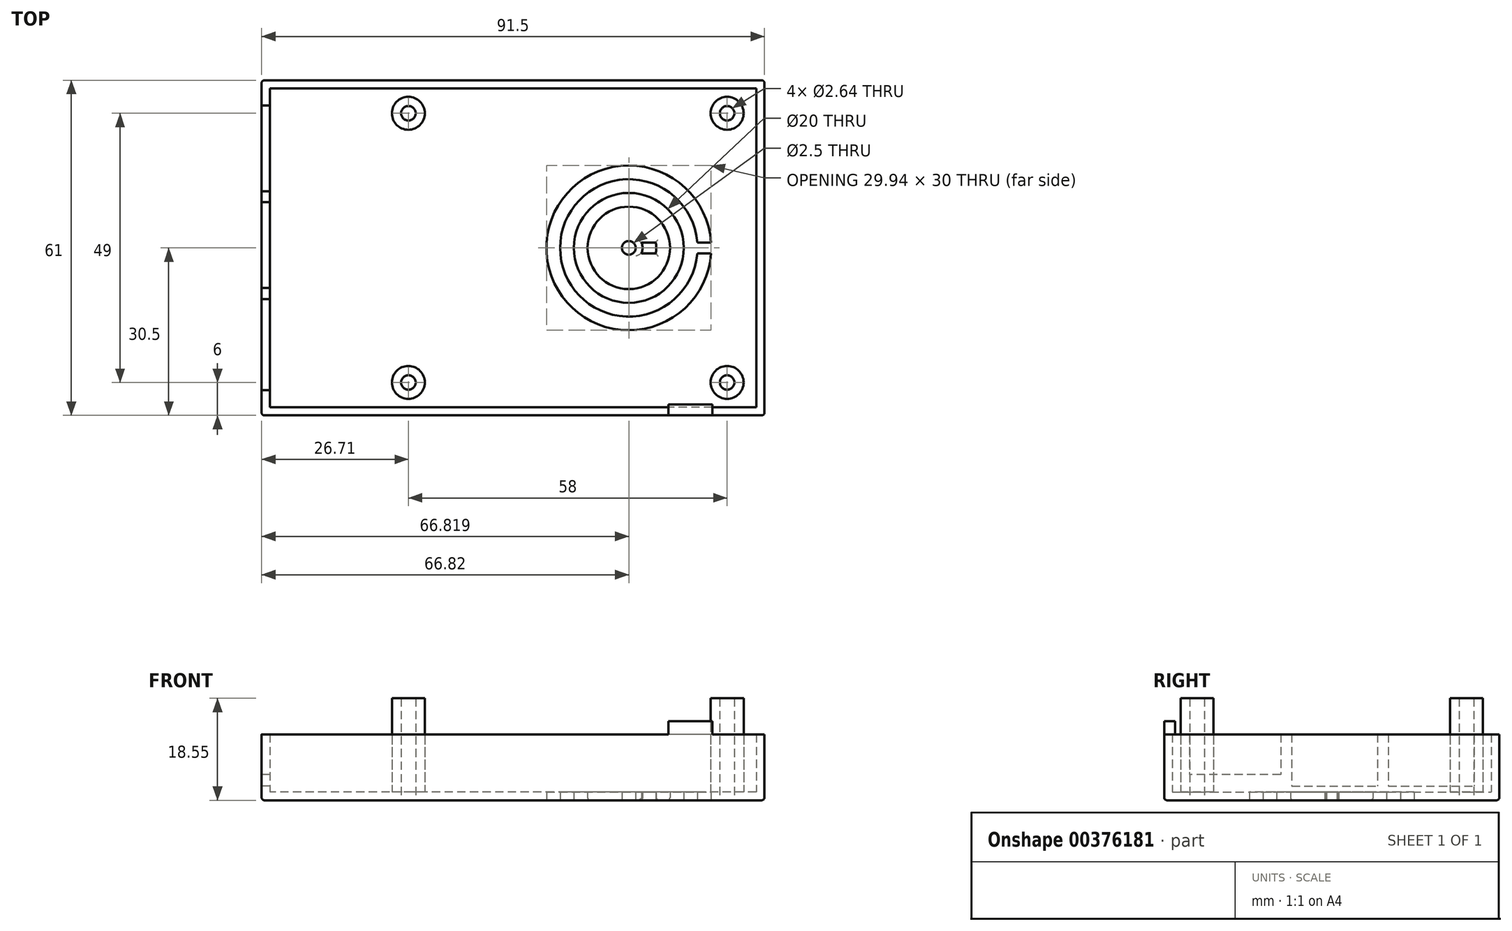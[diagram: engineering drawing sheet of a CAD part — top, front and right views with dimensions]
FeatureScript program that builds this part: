
annotation { "Feature Type Name" : "Feature", "Feature Type Description" : "" }
export const myFeature = defineFeature(function(context is Context, id is Id, definition is map)
    precondition{}
    {
        {
            var Q0;
            Q0=qCreatedBy(makeId("Top.planeOp"),FACE);
            var sketch = newSketch(context, id + "F0", { "sketchPlane" : qUnion([Q0])});
            skLineSegment(sketch, "E0.bottom", {"start": v(45.75, -30.5) * mm, "end": v(-45.75, -30.5) * mm});
            skLineSegment(sketch, "E0.top", {"start": v(45.75, 30.5) * mm, "end": v(-45.75, 30.5) * mm});
            skLineSegment(sketch, "E0.left", {"start": v(45.75, -30.5) * mm, "end": v(45.75, 30.5) * mm});
            skLineSegment(sketch, "E0.right", {"start": v(-45.75, -30.5) * mm, "end": v(-45.75, 30.5) * mm});
            skPoint(sketch, "E0.middle", {"position": v(0, 0) * mm});
            skSolve(sketch);
        }
        {
            var Q0;
            Q0 = qSketchRegion(id + "F0", true);
            extrude(context, id + "F1", {"entities" : qUnion([Q0]), "depth" : 12 * mm});
        }
        {
            var Q0;
            Q0=makeQuery(id+"F1.opExtrude","CAP_FACE",FACE,{"disambiguationData":[OSD([sQuery(id+"F0.wireOp",EDGE,"E0.bottom"),sQuery(id+"F0.wireOp",EDGE,"E0.top"),sQuery(id+"F0.wireOp",EDGE,"E0.left"),sQuery(id+"F0.wireOp",EDGE,"E0.right")])],"isStart":false});
            shell(context, id + "F2", {"entities" : qUnion([Q0]), "thickness" : 1.5 * mm});
        }
        {
            var Q0;
            Q0=makeQuery(id+"F1.opExtrude","SWEPT_FACE",FACE,{"disambiguationData":[OSD([sQuery(id+"F0.wireOp",EDGE,"E0.bottom")])]});
            var sketch = newSketch(context, id + "F3", { "sketchPlane" : qUnion([Q0])});
            skLineSegment(sketch, "E1.bottom", {"start": v(36.25, 12) * mm, "end": v(28.25, 12) * mm});
            skLineSegment(sketch, "E1.top", {"start": v(36.25, 14.4) * mm, "end": v(28.25, 14.4) * mm});
            skLineSegment(sketch, "E1.left", {"start": v(36.25, 12) * mm, "end": v(36.25, 14.4) * mm});
            skLineSegment(sketch, "E1.right", {"start": v(28.25, 12) * mm, "end": v(28.25, 14.4) * mm});
            skSolve(sketch);
        }
        {
            var Q0;
            Q0 = qSketchRegion(id + "F3", true);
            extrude(context, id + "F4", {"entities" : qUnion([Q0]), "operationType" : NewBodyOperationType.ADD, "oppositeDirection" : true, "depth" : 2 * mm});
        }
        {
            var Q0;
            Q0=makeQuery(id+"F1.opExtrude","SWEPT_FACE",FACE,{"disambiguationData":[OSD([sQuery(id+"F0.wireOp",EDGE,"E0.right")])]});
            var sketch = newSketch(context, id + "F5", { "sketchPlane" : qUnion([Q0])});
            skLineSegment(sketch, "E2.bottom", {"start": v(9.3, 12) * mm, "end": v(25.9, 12) * mm});
            skLineSegment(sketch, "E2.top", {"start": v(9.3, 4.7) * mm, "end": v(25.9, 4.7) * mm});
            skLineSegment(sketch, "E2.left", {"start": v(9.3, 12) * mm, "end": v(9.3, 4.7) * mm});
            skLineSegment(sketch, "E2.right", {"start": v(25.9, 12) * mm, "end": v(25.9, 4.7) * mm});
            skLineSegment(sketch, "E3.bottom", {"start": v(7.3, 12) * mm, "end": v(-8.3, 12) * mm});
            skLineSegment(sketch, "E3.top", {"start": v(7.3, 2.6) * mm, "end": v(-8.3, 2.6) * mm});
            skLineSegment(sketch, "E3.left", {"start": v(7.3, 12) * mm, "end": v(7.3, 2.6) * mm});
            skLineSegment(sketch, "E3.right", {"start": v(-8.3, 12) * mm, "end": v(-8.3, 2.6) * mm});
            skLineSegment(sketch, "E4.bottom", {"start": v(-10.3, 12) * mm, "end": v(-25.9, 12) * mm});
            skLineSegment(sketch, "E4.top", {"start": v(-10.3, 2.6) * mm, "end": v(-25.9, 2.6) * mm});
            skLineSegment(sketch, "E4.left", {"start": v(-10.3, 12) * mm, "end": v(-10.3, 2.6) * mm});
            skLineSegment(sketch, "E4.right", {"start": v(-25.9, 12) * mm, "end": v(-25.9, 2.6) * mm});
            skSolve(sketch);
        }
        {
            var Q0;
            Q0 = qSketchRegion(id + "F5", true);
            extrude(context, id + "F6", {"entities" : qUnion([Q0]), "operationType" : NewBodyOperationType.REMOVE, "oppositeDirection" : true, "depth" : 2.1 * mm});
        }
        {
            var Q0;
            Q0=makeQuery(id+"F1.opExtrude","CAP_FACE",FACE,{"disambiguationData":[OSD([sQuery(id+"F0.wireOp",EDGE,"E0.bottom"),sQuery(id+"F0.wireOp",EDGE,"E0.top"),sQuery(id+"F0.wireOp",EDGE,"E0.left"),sQuery(id+"F0.wireOp",EDGE,"E0.right")])],"isStart":true});
            var sketch = newSketch(context, id + "F7", { "sketchPlane" : qUnion([Q0])});
            skCircle(sketch, "E5", {"center": v(21.07, 0) * mm, "radius": 2.5 * mm});
            skCircle(sketch, "E6", {"center": v(21.07, 0) * mm, "radius": 5 * mm});
            skCircle(sketch, "E7", {"center": v(21.07, 0) * mm, "radius": 7.5 * mm});
            skCircle(sketch, "E8", {"center": v(21.07, 0) * mm, "radius": 10 * mm});
            skCircle(sketch, "E9", {"center": v(21.07, 0) * mm, "radius": 12.5 * mm});
            skCircle(sketch, "E10", {"center": v(21.07, 0) * mm, "radius": 15 * mm});
            skLineSegment(sketch, "E11.bottom", {"start": v(36.04, 0.99) * mm, "end": v(33.53, 0.99) * mm});
            skLineSegment(sketch, "E11.top", {"start": v(36.04, -0.99) * mm, "end": v(33.53, -0.99) * mm});
            skLineSegment(sketch, "E11.left", {"start": v(36.04, 0.99) * mm, "end": v(36.04, -0.99) * mm});
            skLineSegment(sketch, "E11.right", {"start": v(6.1, 0.99) * mm, "end": v(6.1, -0.99) * mm});
            skLineSegment(sketch, "E12.trimOffspring", {"start": v(8.6, 0.99) * mm, "end": v(6.1, 0.99) * mm});
            skLineSegment(sketch, "E13.trimOffspring", {"start": v(8.6, -0.99) * mm, "end": v(6.1, -0.99) * mm});
            skLineSegment(sketch, "E14.trimOffspring", {"start": v(31.02, 0.99) * mm, "end": v(11.12, 0.99) * mm});
            skLineSegment(sketch, "E15.trimOffspring", {"start": v(31.02, -0.99) * mm, "end": v(11.12, -0.99) * mm});
            skSolve(sketch);
        }
        {
            var Q0;
            {var subQ0=sQuery(id+"F7.wireOp",EDGE,"E11.bottom");Q0=makeQuery(id+"F7.imprint","IMPRINT",FACE,{"disambiguationData":[TD([[makeQuery(id+"F7.imprint","IMPRINT",EDGE,{"derivedFrom":subQ0}),-1.0]])]});}
            var Q1;
            {var subQ0=sQuery(id+"F7.wireOp",EDGE,"E11.top");Q1=makeQuery(id+"F7.imprint","IMPRINT",FACE,{"disambiguationData":[TD([[makeQuery(id+"F7.imprint","IMPRINT",EDGE,{"derivedFrom":subQ0}),1.0]])]});}
            var Q2;
            {var subQ0=sQuery(id+"F7.wireOp",EDGE,"E14.trimOffspring");var subQ1=sQuery(id+"F7.wireOp",EDGE,"E7");var subQ2=makeQuery(id+"F7.imprint","INTERSECT",VERTEX,{"disambiguationData":[OD(0.0)],"derivedFrom":[subQ1,subQ0]});Q2=makeQuery(id+"F7.imprint","IMPRINT",FACE,{"disambiguationData":[TD([[makeQuery(id+"F7.imprint","IMPRINT",EDGE,{"disambiguationData":[TD([[subQ2,1.0]])],"derivedFrom":subQ1}),-1.0]])]});}
            var Q3;
            {var subQ0=sQuery(id+"F7.wireOp",EDGE,"E15.trimOffspring");var subQ1=sQuery(id+"F7.wireOp",EDGE,"E7");var subQ2=makeQuery(id+"F7.imprint","INTERSECT",VERTEX,{"disambiguationData":[OD(0.0)],"derivedFrom":[subQ1,subQ0]});Q3=makeQuery(id+"F7.imprint","IMPRINT",FACE,{"disambiguationData":[TD([[makeQuery(id+"F7.imprint","IMPRINT",EDGE,{"disambiguationData":[TD([[subQ2,-1.0]])],"derivedFrom":subQ1}),-1.0]])]});}
            var Q4;
            {var subQ0=sQuery(id+"F7.wireOp",EDGE,"E14.trimOffspring");var subQ1=sQuery(id+"F7.wireOp",EDGE,"E5");var subQ2=makeQuery(id+"F7.imprint","INTERSECT",VERTEX,{"disambiguationData":[OD(0.0)],"derivedFrom":[subQ1,subQ0]});Q4=makeQuery(id+"F7.imprint","IMPRINT",FACE,{"disambiguationData":[TD([[makeQuery(id+"F7.imprint","IMPRINT",EDGE,{"disambiguationData":[TD([[subQ2,1.0]])],"derivedFrom":subQ1}),-1.0]])]});}
            var Q5;
            {var subQ0=sQuery(id+"F7.wireOp",EDGE,"E15.trimOffspring");var subQ1=sQuery(id+"F7.wireOp",EDGE,"E5");var subQ2=makeQuery(id+"F7.imprint","INTERSECT",VERTEX,{"disambiguationData":[OD(0.0)],"derivedFrom":[subQ1,subQ0]});Q5=makeQuery(id+"F7.imprint","IMPRINT",FACE,{"disambiguationData":[TD([[makeQuery(id+"F7.imprint","IMPRINT",EDGE,{"disambiguationData":[TD([[subQ2,-1.0]])],"derivedFrom":subQ1}),-1.0]])]});}
            extrude(context, id + "F8", {"entities" : qUnion([Q0, Q1, Q2, Q3, Q4, Q5]), "operationType" : NewBodyOperationType.REMOVE, "oppositeDirection" : true, "depth" : 3 * mm});
        }
        {
            var Q0;
            Q0=makeQuery(id+"F1.opExtrude","CAP_FACE",FACE,{"disambiguationData":[OSD([sQuery(id+"F0.wireOp",EDGE,"E0.bottom"),sQuery(id+"F0.wireOp",EDGE,"E0.top"),sQuery(id+"F0.wireOp",EDGE,"E0.left"),sQuery(id+"F0.wireOp",EDGE,"E0.right")])],"isStart":true});
            var sketch = newSketch(context, id + "F9", { "sketchPlane" : qUnion([Q0])});
            skCircle(sketch, "E16", {"center": v(21.07, 0) * mm, "radius": 1.25 * mm});
            skSolve(sketch);
        }
        {
            var Q0;
            Q0 = qSketchRegion(id + "F9", true);
            extrude(context, id + "F10", {"entities" : qUnion([Q0]), "operationType" : NewBodyOperationType.REMOVE, "oppositeDirection" : true, "depth" : 3 * mm});
        }
        {
            var Q0;
            Q0=makeQuery(id+"F2.opShell","OFFSET_FACE",FACE,{"disambiguationData":[OSD([sQuery(id+"F0.wireOp",EDGE,"E0.bottom"),sQuery(id+"F0.wireOp",EDGE,"E0.top"),sQuery(id+"F0.wireOp",EDGE,"E0.left"),sQuery(id+"F0.wireOp",EDGE,"E0.right")])]});
            var sketch = newSketch(context, id + "F11", { "sketchPlane" : qUnion([Q0])});
            skCircle(sketch, "E17", {"center": v(38.96, 24.5) * mm, "radius": 3 * mm});
            skCircle(sketch, "E18", {"center": v(38.96, 24.5) * mm, "radius": 1.32 * mm});
            skCircle(sketch, "E19", {"center": v(38.96, -24.5) * mm, "radius": 3 * mm});
            skCircle(sketch, "E20", {"center": v(38.96, -24.5) * mm, "radius": 1.32 * mm});
            skCircle(sketch, "E21", {"center": v(-19.04, 24.5) * mm, "radius": 3 * mm});
            skCircle(sketch, "E22", {"center": v(-19.04, 24.5) * mm, "radius": 1.32 * mm});
            skCircle(sketch, "E23", {"center": v(-19.04, -24.5) * mm, "radius": 3 * mm});
            skCircle(sketch, "E24", {"center": v(-19.04, -24.5) * mm, "radius": 1.32 * mm});
            skSolve(sketch);
        }
        {
            var Q0;
            Q0 = qSketchRegion(id + "F11", true);
            extrude(context, id + "F12", {"entities" : qUnion([Q0]), "operationType" : NewBodyOperationType.ADD, "depth" : 17.05 * mm});
        }
        {
            var Q0;
            Q0=makeQuery(id+"F12.boolean.opBoolean","SPLIT",FACE,{"disambiguationData":[TD([makeQuery(id+"F12.opExtrude","SWEPT_FACE",FACE,{"disambiguationData":[OSD([sQuery(id+"F11.wireOp",EDGE,"E18")])]})])],"derivedFrom":makeQuery(id+"F2.opShell","OFFSET_FACE",FACE,{"disambiguationData":[OSD([sQuery(id+"F0.wireOp",EDGE,"E0.bottom"),sQuery(id+"F0.wireOp",EDGE,"E0.top"),sQuery(id+"F0.wireOp",EDGE,"E0.left"),sQuery(id+"F0.wireOp",EDGE,"E0.right")])]})});
            var Q1;
            Q1=makeQuery(id+"F12.boolean.opBoolean","SPLIT",FACE,{"disambiguationData":[TD([makeQuery(id+"F12.opExtrude","SWEPT_FACE",FACE,{"disambiguationData":[OSD([sQuery(id+"F11.wireOp",EDGE,"E20")])]})])],"derivedFrom":makeQuery(id+"F2.opShell","OFFSET_FACE",FACE,{"disambiguationData":[OSD([sQuery(id+"F0.wireOp",EDGE,"E0.bottom"),sQuery(id+"F0.wireOp",EDGE,"E0.top"),sQuery(id+"F0.wireOp",EDGE,"E0.left"),sQuery(id+"F0.wireOp",EDGE,"E0.right")])]})});
            var Q2;
            Q2=makeQuery(id+"F12.boolean.opBoolean","SPLIT",FACE,{"disambiguationData":[TD([makeQuery(id+"F12.opExtrude","SWEPT_FACE",FACE,{"disambiguationData":[OSD([sQuery(id+"F11.wireOp",EDGE,"E24")])]})])],"derivedFrom":makeQuery(id+"F2.opShell","OFFSET_FACE",FACE,{"disambiguationData":[OSD([sQuery(id+"F0.wireOp",EDGE,"E0.bottom"),sQuery(id+"F0.wireOp",EDGE,"E0.top"),sQuery(id+"F0.wireOp",EDGE,"E0.left"),sQuery(id+"F0.wireOp",EDGE,"E0.right")])]})});
            var Q3;
            Q3=makeQuery(id+"F12.boolean.opBoolean","SPLIT",FACE,{"disambiguationData":[TD([makeQuery(id+"F12.opExtrude","SWEPT_FACE",FACE,{"disambiguationData":[OSD([sQuery(id+"F11.wireOp",EDGE,"E22")])]})])],"derivedFrom":makeQuery(id+"F2.opShell","OFFSET_FACE",FACE,{"disambiguationData":[OSD([sQuery(id+"F0.wireOp",EDGE,"E0.bottom"),sQuery(id+"F0.wireOp",EDGE,"E0.top"),sQuery(id+"F0.wireOp",EDGE,"E0.left"),sQuery(id+"F0.wireOp",EDGE,"E0.right")])]})});
            extrude(context, id + "F13", {"entities" : qUnion([Q0, Q1, Q2, Q3]), "operationType" : NewBodyOperationType.REMOVE, "oppositeDirection" : true, "depth" : 25 * mm});
        }
        {
            var Q0;
            Q0=makeQuery(id+"F1.opExtrude","CAP_EDGE",EDGE,{"disambiguationData":[OSD([sQuery(id+"F0.wireOp",EDGE,"E0.top")])],"isStart":true});
            var Q1;
            Q1=makeQuery(id+"F1.opExtrude","CAP_EDGE",EDGE,{"disambiguationData":[OSD([sQuery(id+"F0.wireOp",EDGE,"E0.left")])],"isStart":true});
            var Q2;
            Q2=makeQuery(id+"F1.opExtrude","CAP_EDGE",EDGE,{"disambiguationData":[OSD([sQuery(id+"F0.wireOp",EDGE,"E0.bottom")])],"isStart":true});
            var Q3;
            Q3=makeQuery(id+"F1.opExtrude","CAP_EDGE",EDGE,{"disambiguationData":[OSD([sQuery(id+"F0.wireOp",EDGE,"E0.right")])],"isStart":true});
            var Q4;
            Q4=makeQuery(id+"F1.opExtrude","SWEPT_EDGE",EDGE,{"disambiguationData":[OSD([sQuery(id+"F0.wireOp",EDGE,"E0.bottom"),sQuery(id+"F0.wireOp",EDGE,"E0.left")])]});
            var Q5;
            Q5=makeQuery(id+"F1.opExtrude","SWEPT_EDGE",EDGE,{"disambiguationData":[OSD([sQuery(id+"F0.wireOp",EDGE,"E0.bottom"),sQuery(id+"F0.wireOp",EDGE,"E0.right")])]});
            var Q6;
            Q6=makeQuery(id+"F1.opExtrude","SWEPT_EDGE",EDGE,{"disambiguationData":[OSD([sQuery(id+"F0.wireOp",EDGE,"E0.top"),sQuery(id+"F0.wireOp",EDGE,"E0.right")])]});
            var Q7;
            Q7=makeQuery(id+"F1.opExtrude","SWEPT_EDGE",EDGE,{"disambiguationData":[OSD([sQuery(id+"F0.wireOp",EDGE,"E0.top"),sQuery(id+"F0.wireOp",EDGE,"E0.left")])]});
            fillet(context, id + "F14", {"entities" : qUnion([Q0, Q1, Q2, Q3, Q4, Q5, Q6, Q7]), "radius" : .5 * mm, "tangentPropagation" : true, "allowEdgeOverflow" : false});
        }
        {
            var Q0;
            {var subQ0=sQuery(id+"F7.wireOp",EDGE,"E10");Q0=makeQuery(id+"F8.boolean.opBoolean","COPY",EDGE,{"derivedFrom":makeQuery(id+"F8.opExtrude","CAP_EDGE",EDGE,{"disambiguationData":[OSD([subQ0]),TDD([makeQuery(id+"F7.imprint","IMPRINT",EDGE,{"disambiguationData":[TD([[makeQuery(id+"F7.imprint","INTERSECT",VERTEX,{"derivedFrom":[subQ0,sQuery(id+"F7.wireOp",EDGE,"E11.top"),sQuery(id+"F7.wireOp",EDGE,"E11.left")]}),1.0]])],"derivedFrom":subQ0})])],"isStart":true})});}
            var Q1;
            {var subQ0=sQuery(id+"F7.wireOp",EDGE,"E10");Q1=makeQuery(id+"F8.boolean.opBoolean","COPY",EDGE,{"derivedFrom":makeQuery(id+"F8.opExtrude","CAP_EDGE",EDGE,{"disambiguationData":[OSD([subQ0]),TDD([makeQuery(id+"F7.imprint","IMPRINT",EDGE,{"disambiguationData":[TD([[makeQuery(id+"F7.imprint","INTERSECT",VERTEX,{"derivedFrom":[subQ0,sQuery(id+"F7.wireOp",EDGE,"E11.bottom"),sQuery(id+"F7.wireOp",EDGE,"E11.left")]}),-1.0]])],"derivedFrom":subQ0})])],"isStart":true})});}
            var Q2;
            Q2=makeQuery(id+"F8.boolean.opBoolean","COPY",EDGE,{"derivedFrom":makeQuery(id+"F8.opExtrude","CAP_EDGE",EDGE,{"disambiguationData":[OSD([sQuery(id+"F7.wireOp",EDGE,"E11.top")])],"isStart":true})});
            var Q3;
            Q3=makeQuery(id+"F8.boolean.opBoolean","COPY",EDGE,{"derivedFrom":makeQuery(id+"F8.opExtrude","CAP_EDGE",EDGE,{"disambiguationData":[OSD([sQuery(id+"F7.wireOp",EDGE,"E11.bottom")])],"isStart":true})});
            var Q4;
            {var subQ0=sQuery(id+"F7.wireOp",EDGE,"E9");Q4=makeQuery(id+"F8.boolean.opBoolean","COPY",EDGE,{"derivedFrom":makeQuery(id+"F8.opExtrude","CAP_EDGE",EDGE,{"disambiguationData":[OSD([subQ0]),TDD([makeQuery(id+"F7.imprint","IMPRINT",EDGE,{"disambiguationData":[TD([[makeQuery(id+"F7.imprint","INTERSECT",VERTEX,{"derivedFrom":[subQ0,sQuery(id+"F7.wireOp",EDGE,"E11.top")]}),1.0]])],"derivedFrom":subQ0})])],"isStart":true})});}
            var Q5;
            {var subQ0=sQuery(id+"F7.wireOp",EDGE,"E9");Q5=makeQuery(id+"F8.boolean.opBoolean","COPY",EDGE,{"derivedFrom":makeQuery(id+"F8.opExtrude","CAP_EDGE",EDGE,{"disambiguationData":[OSD([subQ0]),TDD([makeQuery(id+"F7.imprint","IMPRINT",EDGE,{"disambiguationData":[TD([[makeQuery(id+"F7.imprint","INTERSECT",VERTEX,{"derivedFrom":[subQ0,sQuery(id+"F7.wireOp",EDGE,"E11.bottom")]}),-1.0]])],"derivedFrom":subQ0})])],"isStart":true})});}
            var Q6;
            Q6=makeQuery(id+"F8.boolean.opBoolean","COPY",EDGE,{"derivedFrom":makeQuery(id+"F8.opExtrude","CAP_EDGE",EDGE,{"disambiguationData":[OSD([sQuery(id+"F7.wireOp",EDGE,"E12.trimOffspring")])],"isStart":true})});
            var Q7;
            Q7=makeQuery(id+"F8.boolean.opBoolean","COPY",EDGE,{"derivedFrom":makeQuery(id+"F8.opExtrude","CAP_EDGE",EDGE,{"disambiguationData":[OSD([sQuery(id+"F7.wireOp",EDGE,"E13.trimOffspring")])],"isStart":true})});
            var Q8;
            {var subQ0=sQuery(id+"F7.wireOp",EDGE,"E14.trimOffspring");var subQ1=sQuery(id+"F7.wireOp",EDGE,"E8");Q8=makeQuery(id+"F8.boolean.opBoolean","COPY",EDGE,{"derivedFrom":makeQuery(id+"F8.opExtrude","CAP_EDGE",EDGE,{"disambiguationData":[OSD([subQ1]),TDD([makeQuery(id+"F7.imprint","IMPRINT",EDGE,{"disambiguationData":[TD([[makeQuery(id+"F7.imprint","INTERSECT",VERTEX,{"disambiguationData":[OD(0.0)],"derivedFrom":[subQ1,subQ0]}),-1.0]])],"derivedFrom":subQ1})])],"isStart":true})});}
            var Q9;
            {var subQ0=sQuery(id+"F7.wireOp",EDGE,"E15.trimOffspring");var subQ1=sQuery(id+"F7.wireOp",EDGE,"E8");Q9=makeQuery(id+"F8.boolean.opBoolean","COPY",EDGE,{"derivedFrom":makeQuery(id+"F8.opExtrude","CAP_EDGE",EDGE,{"disambiguationData":[OSD([subQ1]),TDD([makeQuery(id+"F7.imprint","IMPRINT",EDGE,{"disambiguationData":[TD([[makeQuery(id+"F7.imprint","INTERSECT",VERTEX,{"disambiguationData":[OD(0.0)],"derivedFrom":[subQ1,subQ0]}),1.0]])],"derivedFrom":subQ1})])],"isStart":true})});}
            var Q10;
            {var subQ0=sQuery(id+"F7.wireOp",EDGE,"E15.trimOffspring");var subQ1=sQuery(id+"F7.wireOp",EDGE,"E7");Q10=makeQuery(id+"F8.boolean.opBoolean","COPY",EDGE,{"derivedFrom":makeQuery(id+"F8.opExtrude","CAP_EDGE",EDGE,{"disambiguationData":[OSD([subQ1]),TDD([makeQuery(id+"F7.imprint","IMPRINT",EDGE,{"disambiguationData":[TD([[makeQuery(id+"F7.imprint","INTERSECT",VERTEX,{"disambiguationData":[OD(0.0)],"derivedFrom":[subQ1,subQ0]}),-1.0]])],"derivedFrom":subQ1})])],"isStart":true})});}
            var Q11;
            {var subQ0=sQuery(id+"F7.wireOp",EDGE,"E14.trimOffspring");var subQ1=sQuery(id+"F7.wireOp",EDGE,"E7");Q11=makeQuery(id+"F8.boolean.opBoolean","COPY",EDGE,{"derivedFrom":makeQuery(id+"F8.opExtrude","CAP_EDGE",EDGE,{"disambiguationData":[OSD([subQ1]),TDD([makeQuery(id+"F7.imprint","IMPRINT",EDGE,{"disambiguationData":[TD([[makeQuery(id+"F7.imprint","INTERSECT",VERTEX,{"disambiguationData":[OD(0.0)],"derivedFrom":[subQ1,subQ0]}),1.0]])],"derivedFrom":subQ1})])],"isStart":true})});}
            var Q12;
            {var subQ0=sQuery(id+"F7.wireOp",EDGE,"E14.trimOffspring");Q12=makeQuery(id+"F8.boolean.opBoolean","COPY",EDGE,{"derivedFrom":makeQuery(id+"F8.opExtrude","CAP_EDGE",EDGE,{"disambiguationData":[OSD([subQ0]),TDD([makeQuery(id+"F7.imprint","IMPRINT",EDGE,{"disambiguationData":[TD([[makeQuery(id+"F7.imprint","INTERSECT",VERTEX,{"disambiguationData":[OD(1.0)],"derivedFrom":[sQuery(id+"F7.wireOp",EDGE,"E8"),subQ0]}),1.0]])],"derivedFrom":subQ0})])],"isStart":true})});}
            var Q13;
            {var subQ0=sQuery(id+"F7.wireOp",EDGE,"E15.trimOffspring");Q13=makeQuery(id+"F8.boolean.opBoolean","COPY",EDGE,{"derivedFrom":makeQuery(id+"F8.opExtrude","CAP_EDGE",EDGE,{"disambiguationData":[OSD([subQ0]),TDD([makeQuery(id+"F7.imprint","IMPRINT",EDGE,{"disambiguationData":[TD([[makeQuery(id+"F7.imprint","INTERSECT",VERTEX,{"disambiguationData":[OD(1.0)],"derivedFrom":[sQuery(id+"F7.wireOp",EDGE,"E8"),subQ0]}),1.0]])],"derivedFrom":subQ0})])],"isStart":true})});}
            var Q14;
            {var subQ0=sQuery(id+"F7.wireOp",EDGE,"E15.trimOffspring");var subQ1=sQuery(id+"F7.wireOp",EDGE,"E6");Q14=makeQuery(id+"F8.boolean.opBoolean","COPY",EDGE,{"derivedFrom":makeQuery(id+"F8.opExtrude","CAP_EDGE",EDGE,{"disambiguationData":[OSD([subQ1]),TDD([makeQuery(id+"F7.imprint","IMPRINT",EDGE,{"disambiguationData":[TD([[makeQuery(id+"F7.imprint","INTERSECT",VERTEX,{"disambiguationData":[OD(0.0)],"derivedFrom":[subQ1,subQ0]}),-1.0]])],"derivedFrom":subQ1})])],"isStart":true})});}
            var Q15;
            {var subQ0=sQuery(id+"F7.wireOp",EDGE,"E15.trimOffspring");Q15=makeQuery(id+"F8.boolean.opBoolean","COPY",EDGE,{"derivedFrom":makeQuery(id+"F8.opExtrude","CAP_EDGE",EDGE,{"disambiguationData":[OSD([subQ0]),TDD([makeQuery(id+"F7.imprint","IMPRINT",EDGE,{"disambiguationData":[TD([[makeQuery(id+"F7.imprint","INTERSECT",VERTEX,{"disambiguationData":[OD(0.0)],"derivedFrom":[sQuery(id+"F7.wireOp",EDGE,"E5"),subQ0]}),-1.0]])],"derivedFrom":subQ0})])],"isStart":true})});}
            var Q16;
            {var subQ0=sQuery(id+"F7.wireOp",EDGE,"E14.trimOffspring");var subQ1=sQuery(id+"F7.wireOp",EDGE,"E6");Q16=makeQuery(id+"F8.boolean.opBoolean","COPY",EDGE,{"derivedFrom":makeQuery(id+"F8.opExtrude","CAP_EDGE",EDGE,{"disambiguationData":[OSD([subQ1]),TDD([makeQuery(id+"F7.imprint","IMPRINT",EDGE,{"disambiguationData":[TD([[makeQuery(id+"F7.imprint","INTERSECT",VERTEX,{"disambiguationData":[OD(0.0)],"derivedFrom":[subQ1,subQ0]}),1.0]])],"derivedFrom":subQ1})])],"isStart":true})});}
            var Q17;
            {var subQ0=sQuery(id+"F7.wireOp",EDGE,"E14.trimOffspring");Q17=makeQuery(id+"F8.boolean.opBoolean","COPY",EDGE,{"derivedFrom":makeQuery(id+"F8.opExtrude","CAP_EDGE",EDGE,{"disambiguationData":[OSD([subQ0]),TDD([makeQuery(id+"F7.imprint","IMPRINT",EDGE,{"disambiguationData":[TD([[makeQuery(id+"F7.imprint","INTERSECT",VERTEX,{"disambiguationData":[OD(0.0)],"derivedFrom":[sQuery(id+"F7.wireOp",EDGE,"E5"),subQ0]}),-1.0]])],"derivedFrom":subQ0})])],"isStart":true})});}
            var Q18;
            {var subQ0=sQuery(id+"F7.wireOp",EDGE,"E14.trimOffspring");Q18=makeQuery(id+"F8.boolean.opBoolean","COPY",EDGE,{"derivedFrom":makeQuery(id+"F8.opExtrude","CAP_EDGE",EDGE,{"disambiguationData":[OSD([subQ0]),TDD([makeQuery(id+"F7.imprint","IMPRINT",EDGE,{"disambiguationData":[TD([[makeQuery(id+"F7.imprint","INTERSECT",VERTEX,{"disambiguationData":[OD(1.0)],"derivedFrom":[sQuery(id+"F7.wireOp",EDGE,"E5"),subQ0]}),1.0]])],"derivedFrom":subQ0})])],"isStart":true})});}
            var Q19;
            {var subQ0=sQuery(id+"F7.wireOp",EDGE,"E15.trimOffspring");Q19=makeQuery(id+"F8.boolean.opBoolean","COPY",EDGE,{"derivedFrom":makeQuery(id+"F8.opExtrude","CAP_EDGE",EDGE,{"disambiguationData":[OSD([subQ0]),TDD([makeQuery(id+"F7.imprint","IMPRINT",EDGE,{"disambiguationData":[TD([[makeQuery(id+"F7.imprint","INTERSECT",VERTEX,{"disambiguationData":[OD(1.0)],"derivedFrom":[sQuery(id+"F7.wireOp",EDGE,"E5"),subQ0]}),1.0]])],"derivedFrom":subQ0})])],"isStart":true})});}
            var Q20;
            {var subQ0=sQuery(id+"F7.wireOp",EDGE,"E15.trimOffspring");Q20=makeQuery(id+"F8.boolean.opBoolean","COPY",EDGE,{"derivedFrom":makeQuery(id+"F8.opExtrude","CAP_EDGE",EDGE,{"disambiguationData":[OSD([subQ0]),TDD([makeQuery(id+"F7.imprint","IMPRINT",EDGE,{"disambiguationData":[TD([[makeQuery(id+"F7.imprint","INTERSECT",VERTEX,{"disambiguationData":[OD(0.0)],"derivedFrom":[sQuery(id+"F7.wireOp",EDGE,"E8"),subQ0]}),-1.0]])],"derivedFrom":subQ0})])],"isStart":true})});}
            var Q21;
            {var subQ0=sQuery(id+"F7.wireOp",EDGE,"E14.trimOffspring");Q21=makeQuery(id+"F8.boolean.opBoolean","COPY",EDGE,{"derivedFrom":makeQuery(id+"F8.opExtrude","CAP_EDGE",EDGE,{"disambiguationData":[OSD([subQ0]),TDD([makeQuery(id+"F7.imprint","IMPRINT",EDGE,{"disambiguationData":[TD([[makeQuery(id+"F7.imprint","INTERSECT",VERTEX,{"disambiguationData":[OD(0.0)],"derivedFrom":[sQuery(id+"F7.wireOp",EDGE,"E8"),subQ0]}),-1.0]])],"derivedFrom":subQ0})])],"isStart":true})});}
            var Q22;
            {var subQ0=sQuery(id+"F7.wireOp",EDGE,"E15.trimOffspring");var subQ1=sQuery(id+"F7.wireOp",EDGE,"E5");Q22=makeQuery(id+"F8.boolean.opBoolean","COPY",EDGE,{"derivedFrom":makeQuery(id+"F8.opExtrude","CAP_EDGE",EDGE,{"disambiguationData":[OSD([subQ1]),TDD([makeQuery(id+"F7.imprint","IMPRINT",EDGE,{"disambiguationData":[TD([[makeQuery(id+"F7.imprint","INTERSECT",VERTEX,{"disambiguationData":[OD(0.0)],"derivedFrom":[subQ1,subQ0]}),-1.0]])],"derivedFrom":subQ1})])],"isStart":true})});}
            var Q23;
            {var subQ0=sQuery(id+"F7.wireOp",EDGE,"E14.trimOffspring");var subQ1=sQuery(id+"F7.wireOp",EDGE,"E5");Q23=makeQuery(id+"F8.boolean.opBoolean","COPY",EDGE,{"derivedFrom":makeQuery(id+"F8.opExtrude","CAP_EDGE",EDGE,{"disambiguationData":[OSD([subQ1]),TDD([makeQuery(id+"F7.imprint","IMPRINT",EDGE,{"disambiguationData":[TD([[makeQuery(id+"F7.imprint","INTERSECT",VERTEX,{"disambiguationData":[OD(0.0)],"derivedFrom":[subQ1,subQ0]}),1.0]])],"derivedFrom":subQ1})])],"isStart":true})});}
            var Q24;
            Q24=makeQuery(id+"F10.boolean.opBoolean","COPY",EDGE,{"derivedFrom":makeQuery(id+"F10.opExtrude","CAP_EDGE",EDGE,{"disambiguationData":[OSD([sQuery(id+"F9.wireOp",EDGE,"E16")])],"isStart":true})});
            fillet(context, id + "F15", {"entities" : qUnion([Q0, Q1, Q2, Q3, Q4, Q5, Q6, Q7, Q8, Q9, Q10, Q11, Q12, Q13, Q14, Q15, Q16, Q17, Q18, Q19, Q20, Q21, Q22, Q23, Q24]), "radius" : .5 * mm, "tangentPropagation" : true, "allowEdgeOverflow" : false});
        }
    });
